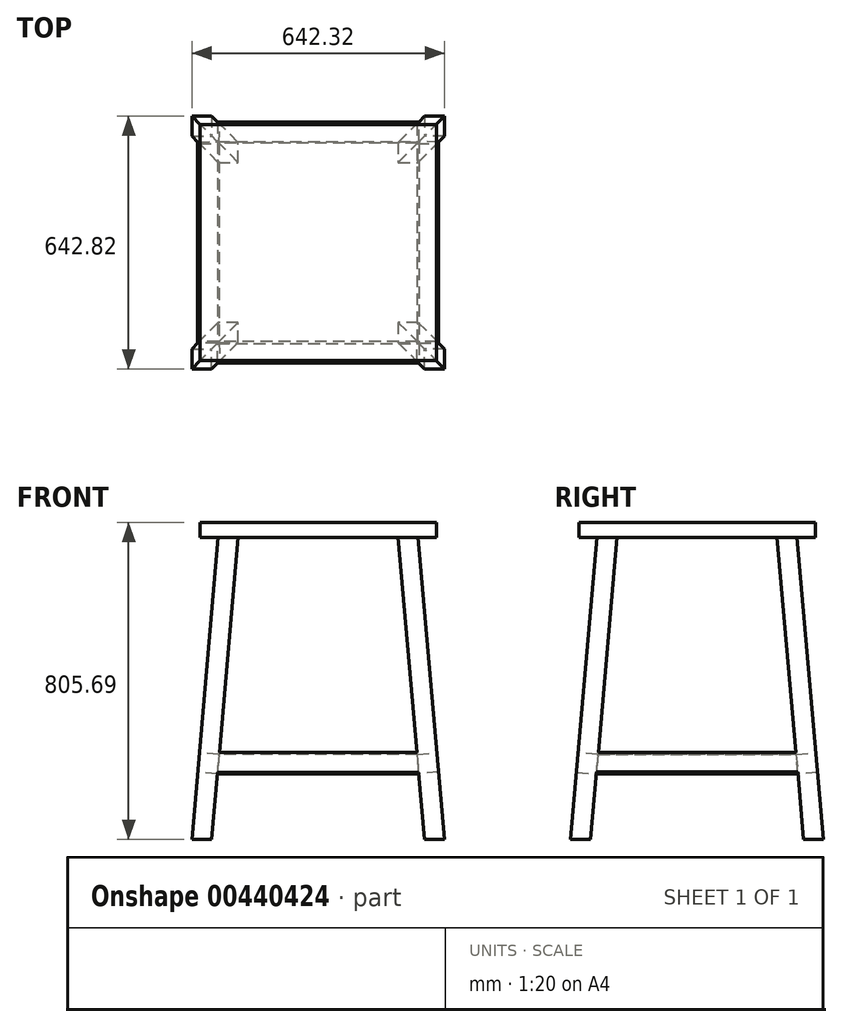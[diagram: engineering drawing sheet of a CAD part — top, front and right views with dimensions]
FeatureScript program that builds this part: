
annotation { "Feature Type Name" : "Feature", "Feature Type Description" : "" }
export const myFeature = defineFeature(function(context is Context, id is Id, definition is map)
    precondition{}
    {
        {
            var Q0;
            Q0=qCreatedBy(makeId("Top.planeOp"),FACE);
            var sketch = newSketch(context, id + "F0", { "sketchPlane" : qUnion([Q0])});
            skLineSegment(sketch, "E0.bottom", {"start": v(300, 300) * mm, "end": v(-300, 300) * mm});
            skLineSegment(sketch, "E0.top", {"start": v(300, -300) * mm, "end": v(-300, -300) * mm});
            skLineSegment(sketch, "E0.left", {"start": v(300, 300) * mm, "end": v(300, -300) * mm});
            skLineSegment(sketch, "E0.right", {"start": v(-300, 300) * mm, "end": v(-300, -300) * mm});
            skPoint(sketch, "E0.middle", {"position": v(0, 0) * mm});
            skSolve(sketch);
        }
        {
            var Q0;
            Q0 = qSketchRegion(id + "F0", true);
            extrude(context, id + "F1", {"entities" : qUnion([Q0]), "depth" : 38.1 * mm});
        }
        {
            var Q0;
            Q0=makeQuery(id+"F1.opExtrude","CAP_FACE",FACE,{"disambiguationData":[OSD([sQuery(id+"F0.wireOp",EDGE,"E0.bottom"),sQuery(id+"F0.wireOp",EDGE,"E0.top"),sQuery(id+"F0.wireOp",EDGE,"E0.left"),sQuery(id+"F0.wireOp",EDGE,"E0.right")])],"isStart":true});
            var sketch = newSketch(context, id + "F2", { "sketchPlane" : qUnion([Q0])});
            skLineSegment(sketch, "E1.bottom", {"start": v(254, 254) * mm, "end": v(203.2, 254) * mm});
            skLineSegment(sketch, "E1.top", {"start": v(254, -254) * mm, "end": v(203.2, -254) * mm});
            skLineSegment(sketch, "E1.right", {"start": v(-254, 254) * mm, "end": v(-254, 203.2) * mm});
            skPoint(sketch, "E1.middle", {"position": v(0, 0) * mm});
            skLineSegment(sketch, "E2.bottom", {"start": v(-254, 254) * mm, "end": v(-203.2, 254) * mm});
            skLineSegment(sketch, "E2.top", {"start": v(-254, 203.2) * mm, "end": v(-203.2, 203.2) * mm});
            skLineSegment(sketch, "E2.right", {"start": v(-203.2, 254) * mm, "end": v(-203.2, 203.2) * mm});
            skLineSegment(sketch, "E3.top", {"start": v(254, 203.2) * mm, "end": v(203.2, 203.2) * mm});
            skLineSegment(sketch, "E3.left", {"start": v(254, 254) * mm, "end": v(254, 203.2) * mm});
            skLineSegment(sketch, "E3.right", {"start": v(203.2, 254) * mm, "end": v(203.2, 203.2) * mm});
            skLineSegment(sketch, "E4.bottom", {"start": v(-254, -254) * mm, "end": v(-203.2, -254) * mm});
            skLineSegment(sketch, "E4.top", {"start": v(-254, -203.2) * mm, "end": v(-203.2, -203.2) * mm});
            skLineSegment(sketch, "E4.left", {"start": v(-254, -254) * mm, "end": v(-254, -203.2) * mm});
            skLineSegment(sketch, "E4.right", {"start": v(-203.2, -254) * mm, "end": v(-203.2, -203.2) * mm});
            skLineSegment(sketch, "E5.top", {"start": v(254, -203.2) * mm, "end": v(203.2, -203.2) * mm});
            skLineSegment(sketch, "E5.left", {"start": v(254, -254) * mm, "end": v(254, -203.2) * mm});
            skLineSegment(sketch, "E5.right", {"start": v(203.2, -254) * mm, "end": v(203.2, -203.2) * mm});
            skLineSegment(sketch, "E6.trimOffspring", {"start": v(-203.2, 254) * mm, "end": v(-254, 254) * mm});
            skLineSegment(sketch, "E7.trimOffspring", {"start": v(-254, -203.2) * mm, "end": v(-254, -254) * mm});
            skLineSegment(sketch, "E8.trimOffspring", {"start": v(-203.2, -254) * mm, "end": v(-254, -254) * mm});
            skLineSegment(sketch, "E9.trimOffspring", {"start": v(254, -203.2) * mm, "end": v(254, -254) * mm});
            skSolve(sketch);
        }
        {
            var Q0;
            Q0=qCreatedBy(makeId("Right.planeOp"),FACE);
            var Q1;
            Q1=makeQuery(id+"F1.opExtrude","CAP_EDGE",EDGE,{"disambiguationData":[OSD([sQuery(id+"F0.wireOp",EDGE,"E0.right")])],"isStart":false});
            cPlane(context, id + "F3", {"entities" : qUnion([Q0, Q1]), "cplaneType" : CPlaneType.LINE_ANGLE, "offset" : 25 * mm, "angle" : 5 * degree, "oppositeDirection" : true, "width" : 150 * mm, "height" : 150 * mm});
        }
        {
            var Q0;
            Q0=qCreatedBy(id+"F3.planeOp",FACE);
            var sketch = newSketch(context, id + "F4", { "sketchPlane" : qUnion([Q0])});
            skLineSegment(sketch, "E10", {"start": v(0, 0) * mm, "end": v(0, -768.61) * mm, "construction": true});
            skLineSegment(sketch, "E11", {"start": v(0, 0) * mm, "end": v(69.72, -796.96) * mm});
            skLineSegment(sketch, "E12", {"start": v(0, 0) * mm, "end": v(-69.72, -796.96) * mm});
            skSolve(sketch);
        }
        {
            var Q0;
            Q0=makeQuery(id+"F2.imprint","IMPRINT",FACE,{"disambiguationData":[TD([[makeQuery(id+"F2.imprint","IMPRINT",EDGE,{"derivedFrom":sQuery(id+"F2.wireOp",EDGE,"E2.top")}),1.0]])]});
            var Q1;
            Q1=sQuery(id+"F4.wireOp",EDGE,"E11");
            sweep(context, id + "F5", {"operationType" : NewBodyOperationType.ADD, "profiles" : qUnion([Q0]), "path" : qUnion([Q1])});
        }
        {
            var Q0;
            Q0=makeQuery(id+"F2.imprint","IMPRINT",FACE,{"disambiguationData":[TD([[makeQuery(id+"F2.imprint","IMPRINT",EDGE,{"derivedFrom":sQuery(id+"F2.wireOp",EDGE,"E4.top")}),-1.0]])]});
            var Q1;
            Q1=sQuery(id+"F4.wireOp",EDGE,"E12");
            sweep(context, id + "F6", {"operationType" : NewBodyOperationType.ADD, "profiles" : qUnion([Q0]), "path" : qUnion([Q1])});
        }
        {
            var Q0;
            Q0=qCreatedBy(makeId("Right.planeOp"),FACE);
            var Q1;
            Q1=makeQuery(id+"F1.opExtrude","CAP_EDGE",EDGE,{"disambiguationData":[OSD([sQuery(id+"F0.wireOp",EDGE,"E0.left")])],"isStart":false});
            cPlane(context, id + "F7", {"entities" : qUnion([Q0, Q1]), "cplaneType" : CPlaneType.LINE_ANGLE, "offset" : 25 * mm, "angle" : 5 * degree, "width" : 150 * mm, "height" : 150 * mm});
        }
        {
            var Q0;
            Q0=qCreatedBy(id+"F7.planeOp",FACE);
            var sketch = newSketch(context, id + "F8", { "sketchPlane" : qUnion([Q0])});
            skLineSegment(sketch, "E13", {"start": v(0, -20.4) * mm, "end": v(0, -772.12) * mm, "construction": true});
            skLineSegment(sketch, "E14", {"start": v(0, 0) * mm, "end": v(-69.72, -796.96) * mm});
            skLineSegment(sketch, "E15", {"start": v(0, 0) * mm, "end": v(69.72, -796.96) * mm});
            skSolve(sketch);
        }
        {
            var Q0;
            Q0=makeQuery(id+"F2.imprint","IMPRINT",FACE,{"disambiguationData":[TD([[makeQuery(id+"F2.imprint","IMPRINT",EDGE,{"derivedFrom":sQuery(id+"F2.wireOp",EDGE,"E1.top")}),-1.0]])]});
            var Q1;
            Q1=sQuery(id+"F8.wireOp",EDGE,"E14");
            sweep(context, id + "F9", {"operationType" : NewBodyOperationType.ADD, "profiles" : qUnion([Q0]), "path" : qUnion([Q1])});
        }
        {
            var Q0;
            Q0=makeQuery(id+"F2.imprint","IMPRINT",FACE,{"disambiguationData":[TD([[makeQuery(id+"F2.imprint","IMPRINT",EDGE,{"derivedFrom":sQuery(id+"F2.wireOp",EDGE,"E1.bottom")}),1.0]])]});
            var Q1;
            Q1=sQuery(id+"F8.wireOp",EDGE,"E15");
            sweep(context, id + "F10", {"operationType" : NewBodyOperationType.ADD, "profiles" : qUnion([Q0]), "path" : qUnion([Q1])});
        }
        {
            var Q0;
            Q0=makeQuery(id+"F5.opSweep","SWEPT_FACE",FACE,{"disambiguationData":[OSD([sQuery(id+"F2.wireOp",EDGE,"E1.right"),sQuery(id+"F4.wireOp",EDGE,"E11")])]});
            var sketch = newSketch(context, id + "F11", { "sketchPlane" : qUnion([Q0])});
            skLineSegment(sketch, "E16", {"start": v(-277.08, -571.34) * mm, "end": v(-277.08, -621.34) * mm});
            skLineSegment(sketch, "E17", {"start": v(-277.08, -621.34) * mm, "end": v(272.92, -621.34) * mm});
            skLineSegment(sketch, "E18", {"start": v(-277.08, -571.34) * mm, "end": v(272.92, -571.34) * mm});
            skLineSegment(sketch, "E19", {"start": v(272.92, -571.34) * mm, "end": v(272.92, -621.34) * mm});
            skPoint(sketch, "E20.start.orphan", {"position": v(-165.42, -571.34) * mm});
            skPoint(sketch, "E21.end.orphan", {"position": v(-165.42, -66.9) * mm});
            skPoint(sketch, "E22.start.orphan", {"position": v(0, 0) * mm});
            skLineSegment(sketch, "E23", {"start": v(0, -21.35) * mm, "end": v(-2.08, -571.34) * mm, "construction": true});
            skPoint(sketch, "E23.endSnap0", {"position": v(-2.08, -621.34) * mm});
            skSolve(sketch);
        }
        {
            var Q0;
            Q0 = qSketchRegion(id + "F11", true);
            extrude(context, id + "F12", {"entities" : qUnion([Q0]), "operationType" : NewBodyOperationType.ADD, "oppositeDirection" : true, "depth" : 50 * mm});
        }
        {
            var Q0;
            Q0=makeQuery(id+"F5.opSweep","SWEPT_FACE",FACE,{"disambiguationData":[OSD([sQuery(id+"F2.wireOp",EDGE,"E6.trimOffspring"),sQuery(id+"F4.wireOp",EDGE,"E11")])]});
            var sketch = newSketch(context, id + "F13", { "sketchPlane" : qUnion([Q0])});
            skLineSegment(sketch, "E24", {"start": v(-272.07, -570.86) * mm, "end": v(-272.07, -620.86) * mm});
            skLineSegment(sketch, "E25", {"start": v(-272.07, -620.86) * mm, "end": v(272.07, -620.86) * mm});
            skLineSegment(sketch, "E26", {"start": v(272.07, -620.86) * mm, "end": v(272.07, -570.86) * mm});
            skLineSegment(sketch, "E27", {"start": v(272.07, -570.86) * mm, "end": v(-272.07, -570.86) * mm});
            skLineSegment(sketch, "E28", {"start": v(0, -20.86) * mm, "end": v(0, -570.86) * mm});
            skSolve(sketch);
        }
        {
            var Q0;
            Q0 = qSketchRegion(id + "F13", true);
            extrude(context, id + "F14", {"entities" : qUnion([Q0]), "operationType" : NewBodyOperationType.ADD, "oppositeDirection" : true, "depth" : 50 * mm});
        }
        {
            var Q0;
            Q0=makeQuery(id+"F10.opSweep","SWEPT_FACE",FACE,{"disambiguationData":[OSD([sQuery(id+"F2.wireOp",EDGE,"E3.left"),sQuery(id+"F8.wireOp",EDGE,"E15")])]});
            var sketch = newSketch(context, id + "F15", { "sketchPlane" : qUnion([Q0])});
            skLineSegment(sketch, "E29", {"start": v(-272.3, -570.6) * mm, "end": v(277.7, -570.6) * mm});
            skLineSegment(sketch, "E30", {"start": v(277.7, -570.6) * mm, "end": v(277.7, -620.6) * mm});
            skLineSegment(sketch, "E31", {"start": v(277.7, -620.6) * mm, "end": v(-272.3, -620.6) * mm});
            skLineSegment(sketch, "E32", {"start": v(-272.3, -620.6) * mm, "end": v(-272.3, -570.6) * mm});
            skLineSegment(sketch, "E33", {"start": v(0, -20.6) * mm, "end": v(2.7, -570.6) * mm});
            skPoint(sketch, "E33.endSnap0", {"position": v(2.7, -570.6) * mm});
            skSolve(sketch);
        }
        {
            var Q0;
            Q0 = qSketchRegion(id + "F15", true);
            extrude(context, id + "F16", {"entities" : qUnion([Q0]), "operationType" : NewBodyOperationType.ADD, "oppositeDirection" : true, "depth" : 50 * mm});
        }
        {
            var Q0;
            Q0=makeQuery(id+"F9.opSweep","SWEPT_FACE",FACE,{"disambiguationData":[OSD([sQuery(id+"F2.wireOp",EDGE,"E1.top"),sQuery(id+"F8.wireOp",EDGE,"E14")])]});
            var sketch = newSketch(context, id + "F17", { "sketchPlane" : qUnion([Q0])});
            skLineSegment(sketch, "E34", {"start": v(-282.73, -571.48) * mm, "end": v(267.27, -571.48) * mm});
            skLineSegment(sketch, "E35", {"start": v(267.27, -571.48) * mm, "end": v(267.27, -621.48) * mm});
            skLineSegment(sketch, "E36", {"start": v(267.27, -621.48) * mm, "end": v(-282.73, -621.48) * mm});
            skLineSegment(sketch, "E37", {"start": v(-282.73, -621.48) * mm, "end": v(-282.73, -571.48) * mm});
            skLineSegment(sketch, "E38", {"start": v(0, -21.48) * mm, "end": v(0, -571.48) * mm});
            skSolve(sketch);
        }
        {
            var Q0;
            Q0 = qSketchRegion(id + "F17", true);
            extrude(context, id + "F18", {"entities" : qUnion([Q0]), "operationType" : NewBodyOperationType.ADD, "oppositeDirection" : true, "depth" : 50 * mm});
        }
    });
